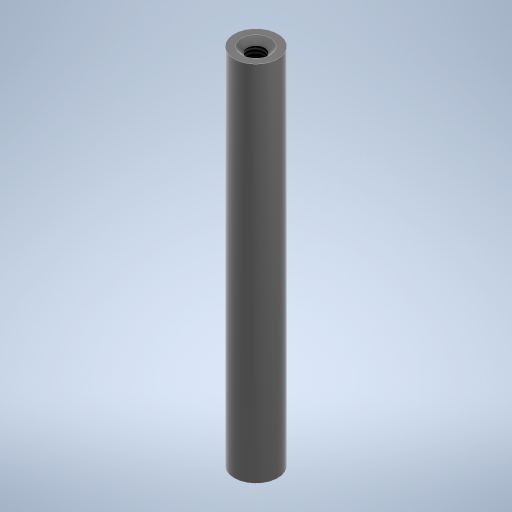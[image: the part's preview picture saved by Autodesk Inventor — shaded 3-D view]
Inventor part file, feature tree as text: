
AUTODESK INVENTOR PART (.ipt)
format: ipt  version: 2024.2 (Build 282272000, 272)  size: 255,488 bytes
history: native  units: mm
features: sketch x2, revolve x1, hole x1, plane x1, mirror x1
ambient origin geometry x8: Origin, YZ Plane, XZ Plane, XY Plane, X Axis, Y Axis, Z Axis, Center Point
bodies: Solid1 (feature_tree)
feature tree (6):
  revolve  "Revolution1"  [1 undecoded]
  hole  "Hole1"  [1 undecoded]
  plane  "Work Plane1"
  mirror  "Mirror1"
  sketch  "Sketch1"  dims[d0=50.0mm d1=6.0mm]
  sketch  "Sketch2"  dims[d2=90.0deg d3=2.459mm d4=6.0mm d5=4.0mm d6=2.0mm d7=90.0deg d8=6.0mm d9=20.594885mm]
note: 2 required parameter values undecoded (feature->parameter linkage not recoverable at this tier; creation-order binding heuristic only, values carry confidence <= 0.55)